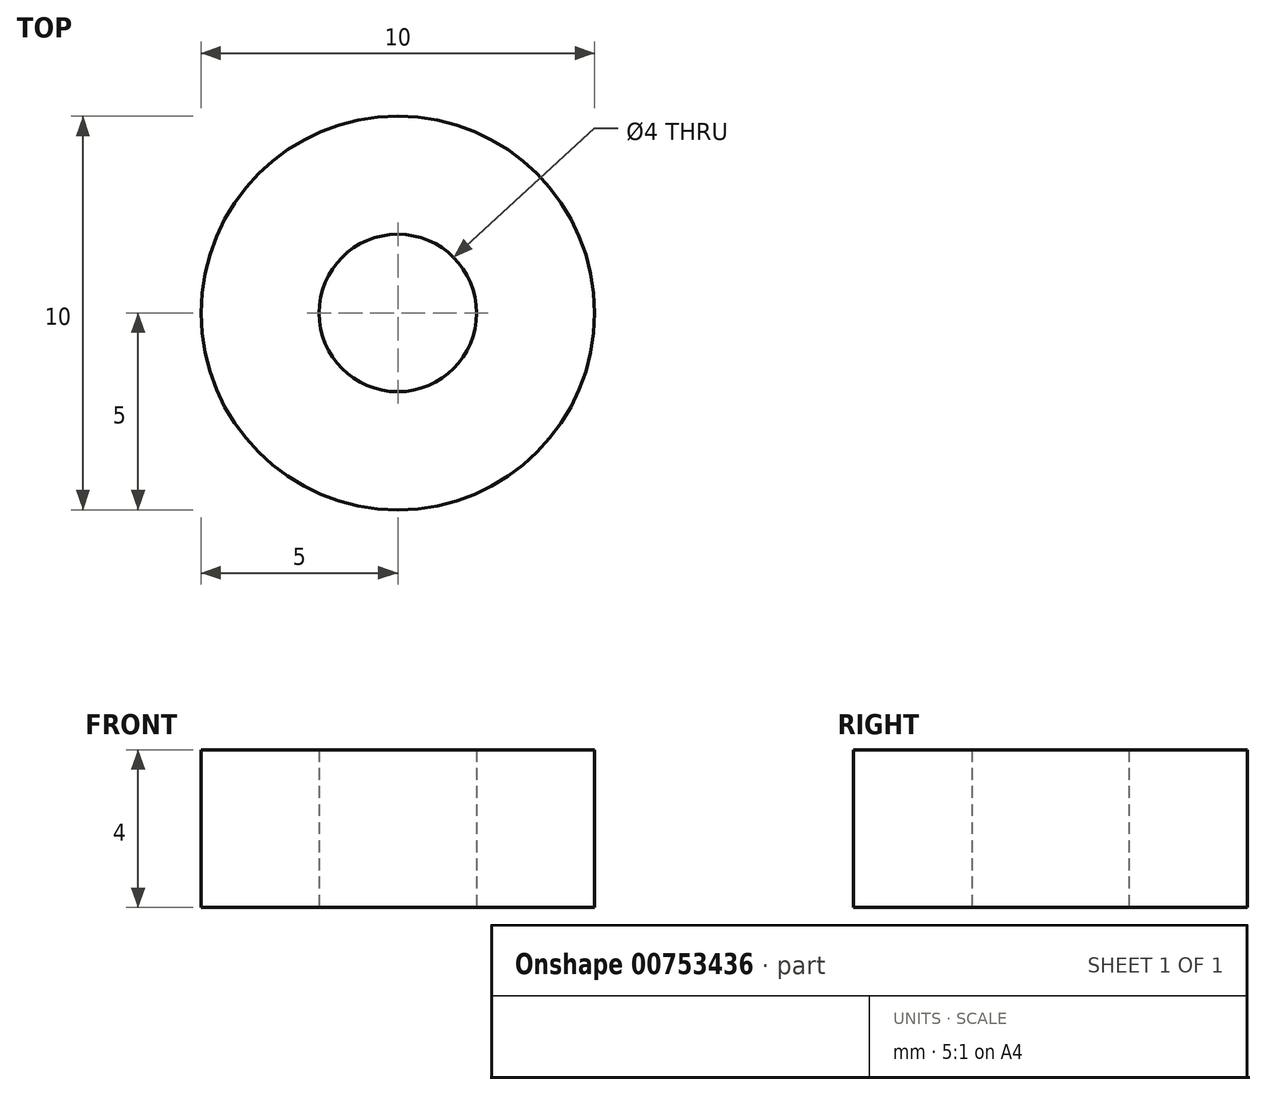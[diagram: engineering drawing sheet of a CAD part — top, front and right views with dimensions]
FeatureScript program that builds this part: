
annotation { "Feature Type Name" : "Feature", "Feature Type Description" : "" }
export const myFeature = defineFeature(function(context is Context, id is Id, definition is map)
    precondition{}
    {
        {
            var Q0;
            Q0=qCreatedBy(makeId("Top.planeOp"),FACE);
            var sketch = newSketch(context, id + "F0", { "sketchPlane" : qUnion([Q0])});
            skCircle(sketch, "E0", {"center": v(0, 0) * mm, "radius": 5 * mm});
            skCircle(sketch, "E1", {"center": v(0, 0) * mm, "radius": 2 * mm});
            skSolve(sketch);
        }
        {
            var Q0;
            Q0=makeQuery(id+"F0.imprint","IMPRINT",FACE,{"disambiguationData":[TD([[makeQuery(id+"F0.imprint","IMPRINT",EDGE,{"derivedFrom":sQuery(id+"F0.wireOp",EDGE,"E0")}),1.0]])]});
            extrude(context, id + "F1", {"entities" : qUnion([Q0]), "depth" : 4 * mm, "offsetDistance" : 25 * mm});
        }
    });
